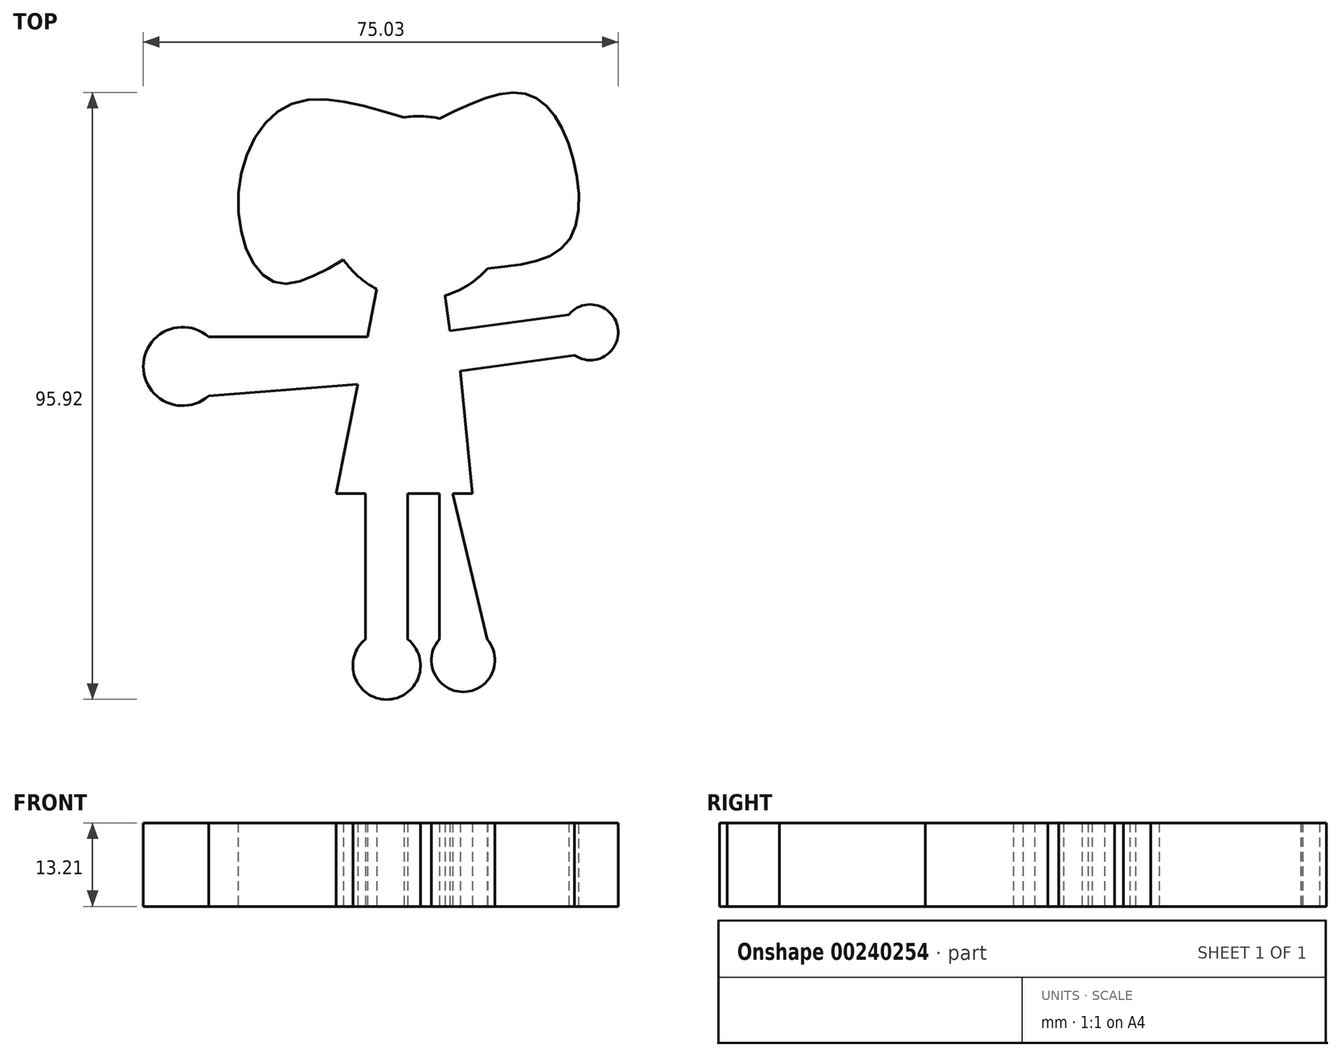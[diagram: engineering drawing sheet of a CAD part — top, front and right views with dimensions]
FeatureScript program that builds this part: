
annotation { "Feature Type Name" : "Feature", "Feature Type Description" : "" }
export const myFeature = defineFeature(function(context is Context, id is Id, definition is map)
    precondition{}
    {
        {
            var Q0;
            Q0=qCreatedBy(makeId("Top.planeOp"),FACE);
            var sketch = newSketch(context, id + "F0", { "sketchPlane" : qUnion([Q0])});
            skArc(sketch, "E0", {"start": v(0.91, 19.5) * mm, "mid": v(4.58, 21.18) * mm, "end": v(7.64, 23.8) * mm});
            skFitSpline(sketch, "E1", {"points": [v(-5.57, 47.65) * mm, v(-24.2, 49.4) * mm, v(-31.77, 34.25) * mm, v(-26.23, 21.71) * mm, v(-15.13, 25.17) * mm], "startDerivative": vector(-74.05, 22.74) * mm, "endDerivative": vector(54.9, 31.98) * mm});
            skFitSpline(sketch, "E2", {"points": [v(0, 47.49) * mm, v(13.4, 51.45) * mm, v(20.4, 43.58) * mm, v(20.4, 28.13) * mm, v(7.64, 23.8) * mm], "startDerivative": vector(56.95, 27.63) * mm, "endDerivative": vector(-61.87, -6.05) * mm});
            skLineSegment(sketch, "E3", {"start": v(-9.86, 20.52) * mm, "end": v(-11.37, 12.97) * mm});
            skLineSegment(sketch, "E4", {"start": v(-16.32, -11.8) * mm, "end": v(-11.66, -11.8) * mm});
            skPoint(sketch, "E5.orphan", {"position": v(0, 26.09) * mm});
            skLineSegment(sketch, "E6", {"start": v(-11.66, -11.8) * mm, "end": v(-11.66, -34.83) * mm});
            skLineSegment(sketch, "E7", {"start": v(-11.66, -34.83) * mm, "end": v(-4.96, -34.83) * mm});
            skLineSegment(sketch, "E8", {"start": v(-4.96, -34.83) * mm, "end": v(-4.96, -11.8) * mm});
            skLineSegment(sketch, "E9", {"start": v(-4.96, -11.8) * mm, "end": v(0, -11.8) * mm});
            skLineSegment(sketch, "E10", {"start": v(0, -11.8) * mm, "end": v(-4.96, -11.8) * mm});
            skLineSegment(sketch, "E11", {"start": v(0, -11.8) * mm, "end": v(0, -34.83) * mm});
            skLineSegment(sketch, "E12", {"start": v(0, -34.83) * mm, "end": v(7.58, -34.83) * mm});
            skLineSegment(sketch, "E13", {"start": v(7.58, -34.83) * mm, "end": v(2.14, -11.8) * mm});
            skArc(sketch, "E14", {"start": v(-11.66, -34.83) * mm, "mid": v(-8.3, -44.33) * mm, "end": v(-4.96, -34.83) * mm});
            skArc(sketch, "E15", {"start": v(0, -34.83) * mm, "mid": v(3.79, -43.13) * mm, "end": v(7.58, -34.83) * mm});
            skLineSegment(sketch, "E16", {"start": v(1.69, 13.9) * mm, "end": v(20.49, 16.5) * mm});
            skLineSegment(sketch, "E17", {"start": v(20.49, 16.5) * mm, "end": v(21.38, 10.07) * mm});
            skLineSegment(sketch, "E18", {"start": v(21.38, 10.07) * mm, "end": v(3.32, 7.57) * mm});
            skLineSegment(sketch, "E19", {"start": v(-11.37, 12.97) * mm, "end": v(-36.43, 12.97) * mm});
            skLineSegment(sketch, "E20", {"start": v(-36.43, 12.97) * mm, "end": v(-36.43, 3.64) * mm});
            skLineSegment(sketch, "E21", {"start": v(-36.43, 3.64) * mm, "end": v(-12.86, 5.5) * mm});
            skArc(sketch, "E22", {"start": v(-36.43, 12.97) * mm, "mid": v(-46.76, 8.3) * mm, "end": v(-36.43, 3.64) * mm});
            skArc(sketch, "E23", {"start": v(21.38, 10.07) * mm, "mid": v(28.23, 14.3) * mm, "end": v(20.49, 16.5) * mm});
            skLineSegment(sketch, "E24.trimOffspring", {"start": v(-12.86, 5.5) * mm, "end": v(-16.32, -11.8) * mm});
            skLineSegment(sketch, "E25.trimOffspring", {"start": v(1.69, 13.9) * mm, "end": v(0.91, 19.5) * mm});
            skLineSegment(sketch, "E26", {"start": v(3.32, 7.57) * mm, "end": v(5.25, -11.8) * mm});
            skPoint(sketch, "E27.orphan", {"position": v(0, 7.1) * mm});
            skPoint(sketch, "E28.orphan", {"position": v(0, -2.77) * mm});
            skPoint(sketch, "E29.start.orphan", {"position": v(-4.96, -2.77) * mm});
            skArc(sketch, "E30.trimOffspring", {"start": v(-15.13, 25.17) * mm, "mid": v(-12.78, 22.52) * mm, "end": v(-9.86, 20.52) * mm});
            skArc(sketch, "E31.trimOffspring", {"start": v(0, 47.49) * mm, "mid": v(-2.78, 47.84) * mm, "end": v(-5.57, 47.65) * mm});
            skLineSegment(sketch, "E32.trimOffspring", {"start": v(2.14, -11.8) * mm, "end": v(5.25, -11.8) * mm});
            skSolve(sketch);
        }
        {
            var Q0;
            Q0 = qSketchRegion(id + "F0", true);
            extrude(context, id + "F1", {"entities" : qUnion([Q0]), "depth" : 13.2 * mm});
        }
    });
